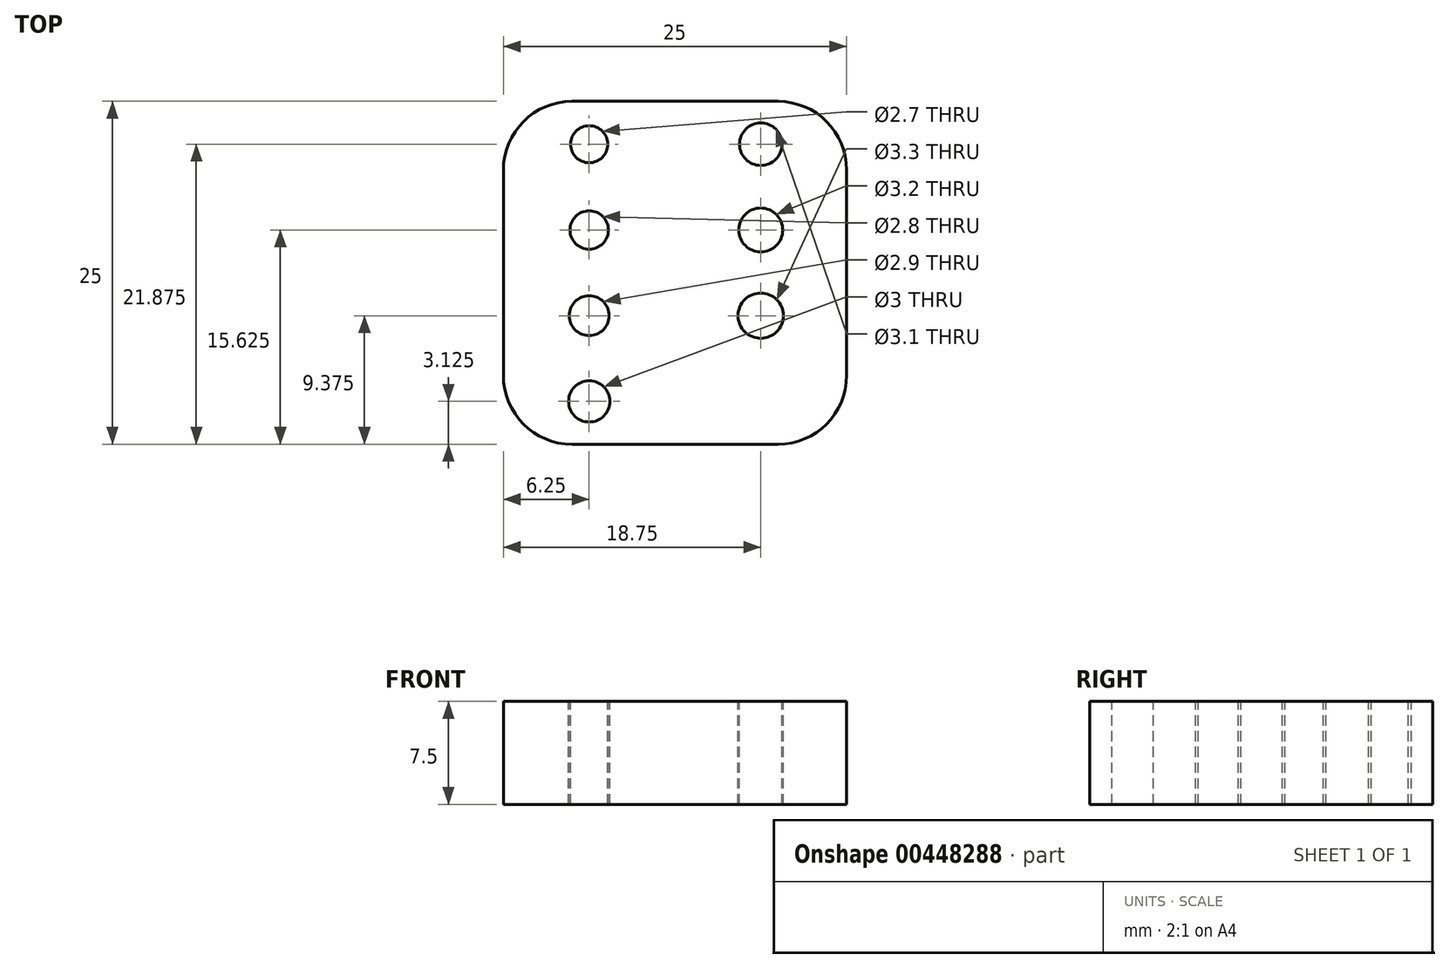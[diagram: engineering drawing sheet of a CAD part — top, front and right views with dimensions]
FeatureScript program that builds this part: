
annotation { "Feature Type Name" : "Feature", "Feature Type Description" : "" }
export const myFeature = defineFeature(function(context is Context, id is Id, definition is map)
    precondition{}
    {
        {
            var Q0;
            Q0=qCreatedBy(makeId("Top.planeOp"),FACE);
            var sketch = newSketch(context, id + "F0", { "sketchPlane" : qUnion([Q0])});
            skLineSegment(sketch, "E0.bottom", {"start": v(12.5, 12.5) * mm, "end": v(-12.5, 12.5) * mm});
            skLineSegment(sketch, "E0.top", {"start": v(12.5, -12.5) * mm, "end": v(-12.5, -12.5) * mm});
            skLineSegment(sketch, "E0.left", {"start": v(12.5, 12.5) * mm, "end": v(12.5, -12.5) * mm});
            skLineSegment(sketch, "E0.right", {"start": v(-12.5, 12.5) * mm, "end": v(-12.5, -12.5) * mm});
            skPoint(sketch, "E0.middle", {"position": v(0, 0) * mm});
            skSolve(sketch);
        }
        {
            var Q0;
            Q0=makeQuery(id+"F0.imprint","IMPRINT",FACE,{"disambiguationData":[TD([[makeQuery(id+"F0.imprint","IMPRINT",EDGE,{"derivedFrom":sQuery(id+"F0.wireOp",EDGE,"E0.bottom")}),1.0]])]});
            extrude(context, id + "F1", {"entities" : qUnion([Q0]), "depth" : 7.5 * mm});
        }
        {
            var Q0;
            Q0=makeQuery(id+"F1.opExtrude","CAP_FACE",FACE,{"disambiguationData":[OSD([sQuery(id+"F0.wireOp",EDGE,"E0.bottom"),sQuery(id+"F0.wireOp",EDGE,"E0.top"),sQuery(id+"F0.wireOp",EDGE,"E0.left"),sQuery(id+"F0.wireOp",EDGE,"E0.right")])],"isStart":false});
            var sketch = newSketch(context, id + "F2", { "sketchPlane" : qUnion([Q0])});
            skLineSegment(sketch, "E1", {"start": v(-12.5, 0) * mm, "end": v(0, 0) * mm, "construction": true});
            skLineSegment(sketch, "E2", {"start": v(0, 0) * mm, "end": v(0, -12.5) * mm, "construction": true});
            skLineSegment(sketch, "E3", {"start": v(0, -12.5) * mm, "end": v(-12.5, -12.5) * mm, "construction": true});
            skLineSegment(sketch, "E4", {"start": v(-12.5, -12.5) * mm, "end": v(-12.5, 0) * mm, "construction": true});
            skLineSegment(sketch, "E5", {"start": v(-6.25, 6.25) * mm, "end": v(-6.25, 12.5) * mm, "construction": true});
            skLineSegment(sketch, "E6", {"start": v(-6.25, 6.25) * mm, "end": v(-6.25, 0) * mm, "construction": true});
            skCircle(sketch, "E7", {"center": v(-6.25, 9.38) * mm, "radius": 1.35 * mm});
            skCircle(sketch, "E8", {"center": v(-6.25, 3.12) * mm, "radius": 1.4 * mm});
            skLineSegment(sketch, "E9", {"start": v(-6.25, 0) * mm, "end": v(-6.25, -6.25) * mm, "construction": true});
            skLineSegment(sketch, "E10", {"start": v(-6.25, -6.25) * mm, "end": v(-6.25, -12.5) * mm, "construction": true});
            skCircle(sketch, "E11", {"center": v(-6.25, -3.12) * mm, "radius": 1.45 * mm});
            skCircle(sketch, "E12", {"center": v(-6.25, -9.38) * mm, "radius": 1.5 * mm});
            skLineSegment(sketch, "E13", {"start": v(-6.25, 6.25) * mm, "end": v(0, 6.25) * mm, "construction": true});
            skLineSegment(sketch, "E14", {"start": v(0, 6.25) * mm, "end": v(6.25, 6.25) * mm, "construction": true});
            skLineSegment(sketch, "E15", {"start": v(-6.25, 9.38) * mm, "end": v(6.25, 9.38) * mm, "construction": true});
            skLineSegment(sketch, "E16", {"start": v(-6.25, 3.12) * mm, "end": v(6.25, 3.12) * mm, "construction": true});
            skLineSegment(sketch, "E17", {"start": v(6.25, 3.12) * mm, "end": v(6.25, 9.38) * mm, "construction": true});
            skLineSegment(sketch, "E18", {"start": v(-12.5, 0) * mm, "end": v(-12.5, 12.5) * mm, "construction": true});
            skLineSegment(sketch, "E19", {"start": v(-12.5, 12.5) * mm, "end": v(-6.25, 12.5) * mm, "construction": true});
            skLineSegment(sketch, "E20", {"start": v(6.25, 3.12) * mm, "end": v(6.25, -12.5) * mm, "construction": true});
            skLineSegment(sketch, "E21", {"start": v(-6.25, -3.12) * mm, "end": v(6.25, -3.12) * mm, "construction": true});
            skCircle(sketch, "E22", {"center": v(6.25, 9.38) * mm, "radius": 1.55 * mm});
            skCircle(sketch, "E23", {"center": v(6.25, 3.12) * mm, "radius": 1.6 * mm});
            skCircle(sketch, "E24", {"center": v(6.25, -3.12) * mm, "radius": 1.65 * mm});
            skSolve(sketch);
        }
        {
            var Q0;
            Q0 = qSketchRegion(id + "F2", true);
            extrude(context, id + "F3", {"entities" : qUnion([Q0]), "operationType" : NewBodyOperationType.REMOVE, "endBound" : BoundingType.THROUGH_ALL, "oppositeDirection" : true, "depth" : 25 * mm});
        }
        {
            var Q0;
            Q0=makeQuery(id+"F1.opExtrude","SWEPT_EDGE",EDGE,{"disambiguationData":[OSD([sQuery(id+"F0.wireOp",EDGE,"E0.bottom"),sQuery(id+"F0.wireOp",EDGE,"E0.right")])]});
            var Q1;
            Q1=makeQuery(id+"F1.opExtrude","SWEPT_EDGE",EDGE,{"disambiguationData":[OSD([sQuery(id+"F0.wireOp",EDGE,"E0.top"),sQuery(id+"F0.wireOp",EDGE,"E0.right")])]});
            var Q2;
            Q2=makeQuery(id+"F1.opExtrude","SWEPT_EDGE",EDGE,{"disambiguationData":[OSD([sQuery(id+"F0.wireOp",EDGE,"E0.top"),sQuery(id+"F0.wireOp",EDGE,"E0.left")])]});
            var Q3;
            Q3=makeQuery(id+"F1.opExtrude","SWEPT_EDGE",EDGE,{"disambiguationData":[OSD([sQuery(id+"F0.wireOp",EDGE,"E0.bottom"),sQuery(id+"F0.wireOp",EDGE,"E0.left")])]});
            fillet(context, id + "F4", {"entities" : qUnion([Q0, Q1, Q2, Q3]), "radius" : 5 * mm, "tangentPropagation" : true, "allowEdgeOverflow" : false});
        }
    });
